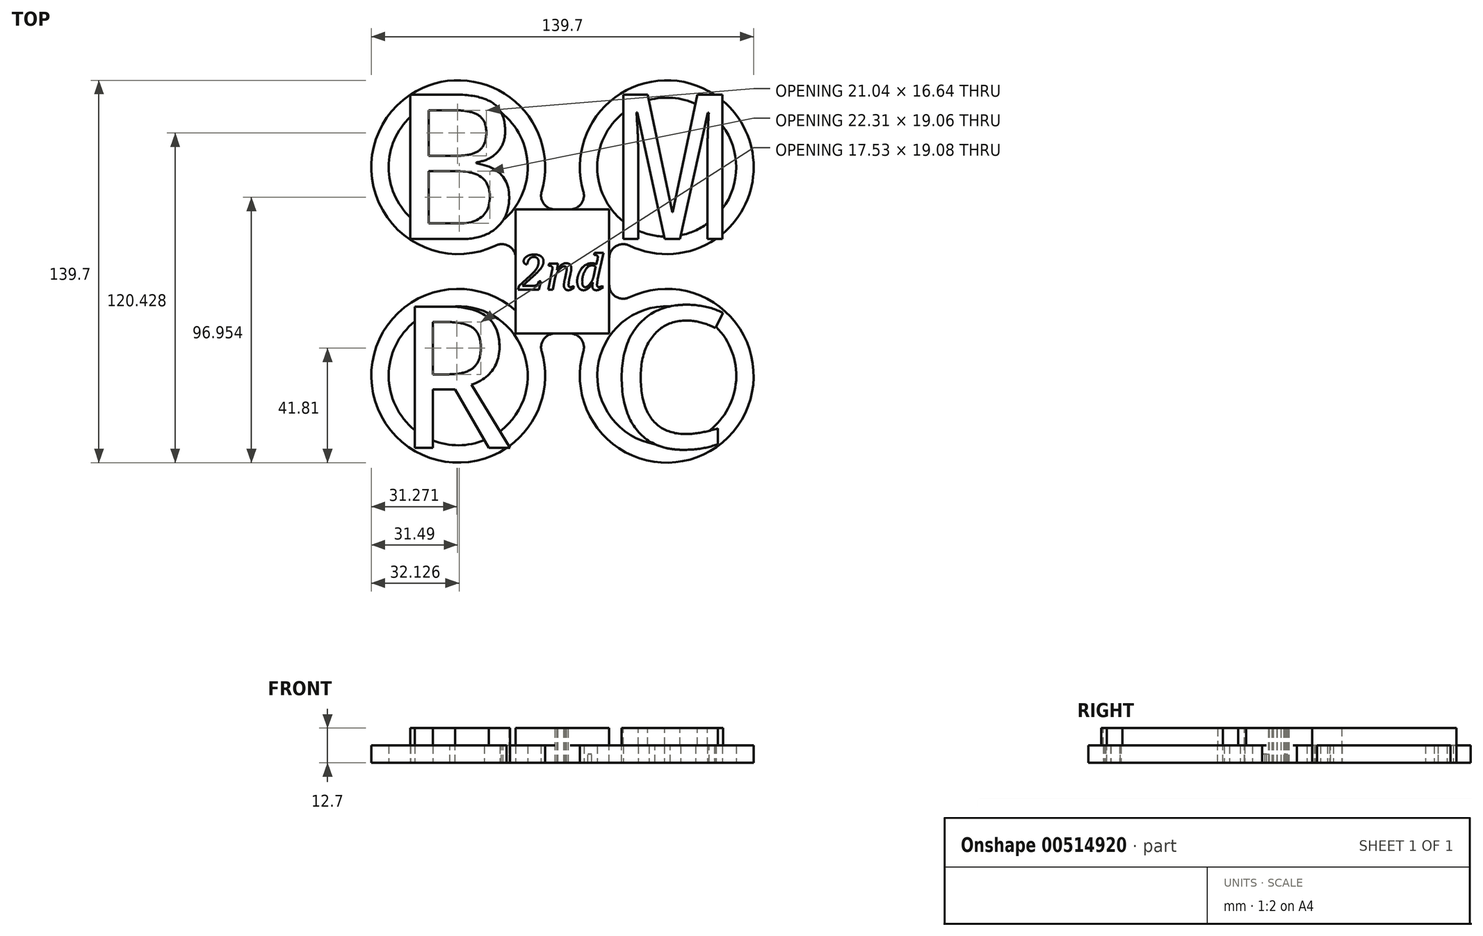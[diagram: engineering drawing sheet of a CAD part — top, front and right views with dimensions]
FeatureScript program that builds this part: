
annotation { "Feature Type Name" : "Feature", "Feature Type Description" : "" }
export const myFeature = defineFeature(function(context is Context, id is Id, definition is map)
    precondition{}
    {
        {
            var Q0;
            Q0=qCreatedBy(makeId("Top.planeOp"),FACE);
            var sketch = newSketch(context, id + "F0", { "sketchPlane" : qUnion([Q0])});
            skLineSegment(sketch, "E0.bottom", {"start": v(38.1, -38.1) * mm, "end": v(-38.1, -38.1) * mm, "construction": true});
            skLineSegment(sketch, "E0.top", {"start": v(38.1, 38.1) * mm, "end": v(-38.1, 38.1) * mm, "construction": true});
            skLineSegment(sketch, "E0.left", {"start": v(38.1, -38.1) * mm, "end": v(38.1, 38.1) * mm, "construction": true});
            skLineSegment(sketch, "E0.right", {"start": v(-38.1, -38.1) * mm, "end": v(-38.1, 38.1) * mm, "construction": true});
            skPoint(sketch, "E0.middle", {"position": v(0, 0) * mm});
            skCircle(sketch, "E1", {"center": v(-38.1, 38.1) * mm, "radius": 31.75 * mm});
            skCircle(sketch, "E2", {"center": v(-38.1, 38.1) * mm, "radius": 25.4 * mm});
            skCircle(sketch, "E3", {"center": v(38.1, 38.1) * mm, "radius": 31.75 * mm});
            skCircle(sketch, "E4", {"center": v(38.1, 38.1) * mm, "radius": 25.4 * mm});
            skCircle(sketch, "E5", {"center": v(-38.1, -38.1) * mm, "radius": 31.75 * mm});
            skCircle(sketch, "E6", {"center": v(-38.1, -38.1) * mm, "radius": 25.4 * mm});
            skCircle(sketch, "E7", {"center": v(38.1, -38.1) * mm, "radius": 31.75 * mm});
            skCircle(sketch, "E8", {"center": v(38.1, -38.1) * mm, "radius": 25.4 * mm});
            skSolve(sketch);
        }
        {
            var Q0;
            Q0=qSketchRegion(id+"F0",true);
            extrude(context, id + "F1", {"entities" : qUnion([Q0]), "depth" : 6.35 * mm, "offsetDistance" : 25.4 * mm});
        }
        {
            var Q0;
            Q0=qCreatedBy(makeId("Top.planeOp"),FACE);
            var sketch = newSketch(context, id + "F2", { "sketchPlane" : qUnion([Q0])});
            skLineSegment(sketch, "E9.bottom", {"start": v(-17.08, -22.68) * mm, "end": v(17.08, -22.68) * mm});
            skLineSegment(sketch, "E9.top", {"start": v(-17.08, 22.68) * mm, "end": v(17.08, 22.68) * mm});
            skLineSegment(sketch, "E9.left", {"start": v(-17.08, -22.68) * mm, "end": v(-17.08, 22.68) * mm});
            skLineSegment(sketch, "E9.right", {"start": v(17.08, -22.68) * mm, "end": v(17.08, 22.68) * mm});
            skPoint(sketch, "E9.middle", {"position": v(0, 0) * mm});
            skSolve(sketch);
        }
        {
            var Q0;
            Q0=qSketchRegion(id+"F2",true);
            extrude(context, id + "F3", {"entities" : qUnion([Q0]), "operationType" : NewBodyOperationType.ADD, "depth" : 12.7 * mm, "offsetDistance" : 25.4 * mm});
        }
        {
            var Q0;
            Q0=makeQuery(id+"F3.opExtrude","CAP_FACE",FACE,{"disambiguationData":[OSD([sQuery(id+"F2.wireOp",EDGE,"E9.bottom"),sQuery(id+"F2.wireOp",EDGE,"E9.top"),sQuery(id+"F2.wireOp",EDGE,"E9.left"),sQuery(id+"F2.wireOp",EDGE,"E9.right")])],"isStart":false});
            var sketch = newSketch(context, id + "F4", { "sketchPlane" : qUnion([Q0])});
            skText(sketch, "E10", { "text": "B", "fontName": "DroidSansMono.ttf"});
            skText(sketch, "E11", { "text": "M", "fontName": "DroidSansMono.ttf"});
            skText(sketch, "E12", { "text": "R", "fontName": "DroidSansMono.ttf"});
            skText(sketch, "E13", { "text": "C", "fontName": "DroidSansMono.ttf"});
            const initialGuessF4  = {"E10": [-0.0605, 0.01187, 1, 0, 0.05322], "E11": [0.01816, 0.01187, 1, 0, 0.05322], "E12": [-0.0605, -0.06445, 1, 0, 0.052], "E13": [0.01708, -0.06445, 1, 0, 0.052]};
            skSetInitialGuess(sketch, initialGuessF4);
            skSolve(sketch);
        }
        {
            var Q0;
            Q0=qSketchRegion(id+"F4",true);
            var Q1;
            Q1=makeQuery(id+"F3.boolean.opBoolean","MERGE",FACE,{"derivedFrom":[makeQuery(id+"F1.opExtrude","CAP_FACE",FACE,{"disambiguationData":[OSD([sQuery(id+"F0.wireOp",EDGE,"E1"),sQuery(id+"F0.wireOp",EDGE,"E2")])],"isStart":true}),makeQuery(id+"F1.opExtrude","CAP_FACE",FACE,{"disambiguationData":[OSD([sQuery(id+"F0.wireOp",EDGE,"E3"),sQuery(id+"F0.wireOp",EDGE,"E4")])],"isStart":true}),makeQuery(id+"F1.opExtrude","CAP_FACE",FACE,{"disambiguationData":[OSD([sQuery(id+"F0.wireOp",EDGE,"E5"),sQuery(id+"F0.wireOp",EDGE,"E6")])],"isStart":true}),makeQuery(id+"F1.opExtrude","CAP_FACE",FACE,{"disambiguationData":[OSD([sQuery(id+"F0.wireOp",EDGE,"E7"),sQuery(id+"F0.wireOp",EDGE,"E8")])],"isStart":true}),makeQuery(id+"F3.opExtrude","CAP_FACE",FACE,{"disambiguationData":[OSD([sQuery(id+"F2.wireOp",EDGE,"E9.bottom"),sQuery(id+"F2.wireOp",EDGE,"E9.top"),sQuery(id+"F2.wireOp",EDGE,"E9.left"),sQuery(id+"F2.wireOp",EDGE,"E9.right")])],"isStart":true})]});
            extrude(context, id + "F5", {"entities" : qUnion([Q0]), "operationType" : NewBodyOperationType.ADD, "endBound" : BoundingType.UP_TO_SURFACE, "oppositeDirection" : true, "depth" : 25.4 * mm, "endBoundEntityFace" : qUnion([Q1]), "offsetDistance" : 25.4 * mm});
        }
        {
            var Q0;
            Q0=makeQuery(id+"F3.opExtrude","CAP_FACE",FACE,{"disambiguationData":[OSD([sQuery(id+"F2.wireOp",EDGE,"E9.bottom"),sQuery(id+"F2.wireOp",EDGE,"E9.top"),sQuery(id+"F2.wireOp",EDGE,"E9.left"),sQuery(id+"F2.wireOp",EDGE,"E9.right")])],"isStart":false});
            var sketch = newSketch(context, id + "F6", { "sketchPlane" : qUnion([Q0])});
            skText(sketch, "E14", { "text": "2nd", "fontName": "NotoSerif-Italic.ttf"});
            const initialGuessF6  = {"E14": [-0.01598, -0.00668, 1, 0, 0.0128]};
            skSetInitialGuess(sketch, initialGuessF6);
            skSolve(sketch);
        }
        {
            var Q0;
            Q0=qSketchRegion(id+"F6",true);
            extrude(context, id + "F7", {"entities" : qUnion([Q0]), "operationType" : NewBodyOperationType.REMOVE, "oppositeDirection" : true, "depth" : 25.4 * mm, "offsetDistance" : 25.4 * mm});
        }
        {
            var Q0;
            {var subQ0=sQuery(id+"F2.wireOp",EDGE,"E9.right");var subQ1=sQuery(id+"F0.wireOp",EDGE,"E8");var subQ2=sQuery(id+"F0.wireOp",EDGE,"E1");var subQ3=sQuery(id+"F0.wireOp",EDGE,"E4");var subQ4=sQuery(id+"F2.wireOp",EDGE,"E9.top");var subQ5=sQuery(id+"F0.wireOp",EDGE,"E2");var subQ6=sQuery(id+"F0.wireOp",EDGE,"E6");var subQ7=sQuery(id+"F2.wireOp",EDGE,"E9.left");var subQ8=sQuery(id+"F0.wireOp",EDGE,"E5");var subQ9=sQuery(id+"F0.wireOp",EDGE,"E7");var subQ10=sQuery(id+"F0.wireOp",EDGE,"E3");var subQ11=sQuery(id+"F2.wireOp",EDGE,"E9.bottom");Q0=makeQuery(id+"F7.boolean.opBoolean","SPLIT",FACE,{"disambiguationData":[TD([makeQuery(id+"F1.opExtrude","SWEPT_FACE",FACE,{"disambiguationData":[OSD([subQ2])]})])],"derivedFrom":makeQuery(id+"F5.boolean.opBoolean","MERGE",FACE,{"derivedFrom":[makeQuery(id+"F3.boolean.opBoolean","MERGE",FACE,{"derivedFrom":[makeQuery(id+"F1.opExtrude","CAP_FACE",FACE,{"disambiguationData":[OSD([subQ2,subQ5])],"isStart":true}),makeQuery(id+"F1.opExtrude","CAP_FACE",FACE,{"disambiguationData":[OSD([subQ10,subQ3])],"isStart":true}),makeQuery(id+"F1.opExtrude","CAP_FACE",FACE,{"disambiguationData":[OSD([subQ8,subQ6])],"isStart":true}),makeQuery(id+"F1.opExtrude","CAP_FACE",FACE,{"disambiguationData":[OSD([subQ9,subQ1])],"isStart":true}),makeQuery(id+"F3.opExtrude","CAP_FACE",FACE,{"disambiguationData":[OSD([subQ11,subQ4,subQ7,subQ0])],"isStart":true})]}),makeQuery(id+"F5.opExtrude","CAP_FACE",FACE,{"disambiguationData":[OSD([subQ2,subQ5,subQ10,subQ3,subQ8,subQ6,subQ9,subQ1,subQ11,subQ4,subQ7,subQ0]),OD(0.0)],"isStart":false}),makeQuery(id+"F5.opExtrude","CAP_FACE",FACE,{"disambiguationData":[OSD([subQ2,subQ5,subQ10,subQ3,subQ8,subQ6,subQ9,subQ1,subQ11,subQ4,subQ7,subQ0]),OD(1.0)],"isStart":false}),makeQuery(id+"F5.opExtrude","CAP_FACE",FACE,{"disambiguationData":[OSD([subQ2,subQ5,subQ10,subQ3,subQ8,subQ6,subQ9,subQ1,subQ11,subQ4,subQ7,subQ0]),OD(2.0)],"isStart":false}),makeQuery(id+"F5.opExtrude","CAP_FACE",FACE,{"disambiguationData":[OSD([subQ2,subQ5,subQ10,subQ3,subQ8,subQ6,subQ9,subQ1,subQ11,subQ4,subQ7,subQ0]),OD(3.0)],"isStart":false})]})});}
            var sketch = newSketch(context, id + "F8", { "sketchPlane" : qUnion([Q0])});
            skLineSegment(sketch, "E15.bottom", {"start": v(9.31, 7.52) * mm, "end": v(10.63, 7.52) * mm});
            skLineSegment(sketch, "E15.top", {"start": v(9.31, 3.1) * mm, "end": v(10.63, 3.1) * mm});
            skLineSegment(sketch, "E15.left", {"start": v(9.31, 7.52) * mm, "end": v(9.31, 3.1) * mm});
            skLineSegment(sketch, "E15.right", {"start": v(10.63, 7.52) * mm, "end": v(10.63, 3.1) * mm});
            skLineSegment(sketch, "E16.bottom", {"start": v(9.31, -0.48) * mm, "end": v(10.63, -0.48) * mm});
            skLineSegment(sketch, "E16.top", {"start": v(9.31, -4.67) * mm, "end": v(10.63, -4.67) * mm});
            skLineSegment(sketch, "E16.left", {"start": v(9.31, -0.48) * mm, "end": v(9.31, -4.67) * mm});
            skLineSegment(sketch, "E16.right", {"start": v(10.63, -0.48) * mm, "end": v(10.63, -4.67) * mm});
            skSolve(sketch);
        }
        {
            var Q0;
            Q0=qSketchRegion(id+"F8",true);
            extrude(context, id + "F9", {"entities" : qUnion([Q0]), "operationType" : NewBodyOperationType.ADD, "oppositeDirection" : true, "depth" : 3.17 * mm, "offsetDistance" : 25.4 * mm});
        }
        {
            var Q0;
            Q0=makeQuery(id+"F3.boolean.opBoolean","INTERSECT",EDGE,{"derivedFrom":[makeQuery(id+"F1.opExtrude","SWEPT_FACE",FACE,{"disambiguationData":[OSD([sQuery(id+"F0.wireOp",EDGE,"E5")])]}),makeQuery(id+"F3.opExtrude","SWEPT_FACE",FACE,{"disambiguationData":[OSD([sQuery(id+"F2.wireOp",EDGE,"E9.bottom")])]})]});
            var Q1;
            Q1=makeQuery(id+"F3.boolean.opBoolean","INTERSECT",EDGE,{"derivedFrom":[makeQuery(id+"F1.opExtrude","SWEPT_FACE",FACE,{"disambiguationData":[OSD([sQuery(id+"F0.wireOp",EDGE,"E7")])]}),makeQuery(id+"F3.opExtrude","SWEPT_FACE",FACE,{"disambiguationData":[OSD([sQuery(id+"F2.wireOp",EDGE,"E9.bottom")])]})]});
            var Q2;
            Q2=makeQuery(id+"F3.boolean.opBoolean","INTERSECT",EDGE,{"derivedFrom":[makeQuery(id+"F1.opExtrude","SWEPT_FACE",FACE,{"disambiguationData":[OSD([sQuery(id+"F0.wireOp",EDGE,"E7")])]}),makeQuery(id+"F3.opExtrude","SWEPT_FACE",FACE,{"disambiguationData":[OSD([sQuery(id+"F2.wireOp",EDGE,"E9.right")])]})]});
            var Q3;
            Q3=makeQuery(id+"F3.boolean.opBoolean","INTERSECT",EDGE,{"derivedFrom":[makeQuery(id+"F1.opExtrude","SWEPT_FACE",FACE,{"disambiguationData":[OSD([sQuery(id+"F0.wireOp",EDGE,"E3")])]}),makeQuery(id+"F3.opExtrude","SWEPT_FACE",FACE,{"disambiguationData":[OSD([sQuery(id+"F2.wireOp",EDGE,"E9.right")])]})]});
            var Q4;
            Q4=makeQuery(id+"F3.boolean.opBoolean","INTERSECT",EDGE,{"derivedFrom":[makeQuery(id+"F1.opExtrude","SWEPT_FACE",FACE,{"disambiguationData":[OSD([sQuery(id+"F0.wireOp",EDGE,"E1")])]}),makeQuery(id+"F3.opExtrude","SWEPT_FACE",FACE,{"disambiguationData":[OSD([sQuery(id+"F2.wireOp",EDGE,"E9.left")])]})]});
            var Q5;
            Q5=makeQuery(id+"F3.boolean.opBoolean","INTERSECT",EDGE,{"derivedFrom":[makeQuery(id+"F1.opExtrude","SWEPT_FACE",FACE,{"disambiguationData":[OSD([sQuery(id+"F0.wireOp",EDGE,"E1")])]}),makeQuery(id+"F3.opExtrude","SWEPT_FACE",FACE,{"disambiguationData":[OSD([sQuery(id+"F2.wireOp",EDGE,"E9.top")])]})]});
            var Q6;
            Q6=makeQuery(id+"F3.boolean.opBoolean","INTERSECT",EDGE,{"derivedFrom":[makeQuery(id+"F1.opExtrude","SWEPT_FACE",FACE,{"disambiguationData":[OSD([sQuery(id+"F0.wireOp",EDGE,"E3")])]}),makeQuery(id+"F3.opExtrude","SWEPT_FACE",FACE,{"disambiguationData":[OSD([sQuery(id+"F2.wireOp",EDGE,"E9.top")])]})]});
            fillet(context, id + "F10", {"entities" : qUnion([Q0, Q1, Q2, Q3, Q4, Q5, Q6]), "radius" : 5.08 * mm, "tangentPropagation" : true, "allowEdgeOverflow" : false});
        }
    });
